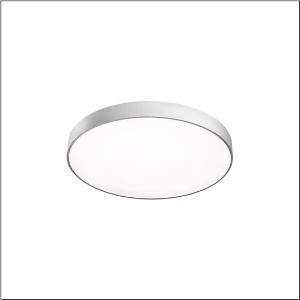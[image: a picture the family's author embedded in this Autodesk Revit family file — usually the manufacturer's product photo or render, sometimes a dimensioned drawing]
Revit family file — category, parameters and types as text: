
# Revit family: round_21_m_51mr36gm8321s
name_source: partatom
category: Lighting Fixtures
units: mm (PartAtom-declared; Revit-internal decimal feet)

## family parameters
Cut with Voids When Loaded = No
Host = Face
Light Source = No
Part Type = Normal
Room Calculation Point = No
Round Connector Dimension = Use Diameter
Shared = No

## types (1)
- --- (1 x LED, 7820 lm, 60.8 W, 3000K)
    Apparent Load = 61 VA
    CIE Flux Codes = 49 80 96 85 100
    Color Rendering = 80
    Color Temperature = 3000K
    Default Elevation = 1800 mm
    Description = Round 21 M, wall and ceiling luminaire, primary optical cover: cover, of PMMA, opal, light emission: direct/indirect distribution, primary light characteristic: symmetric, installation type: suspended mounting, surface-mounted, LED, rated luminous flux: 7.820lm, luminous efficacy: 129lm/W, light colour: 830, colour temperature: 3000K, with terminal, 3-pole, mains connection: 230V, AC, 50/60Hz, rated input power: 61W, housing, of aluminium, coated, silver, diameter: 600mm, height: 62mm, protection rating (complete): IP40, insulation class (complete): insulation class I (protective earthing), certification: CE, impact resistance: IK04, permissible operating ambient temperature: -10..+35°C, packaging unit: 1 piece
    Height = 87 mm
    Lamp = 1 x LED
    Lamp Light Flux = 7820 lm
    Lamp Power = 60.8 W
    Lamp count = 1
    Length = 600 mm
    Luminous efficacy = 129 lm/W
    Manufacturer = Siteco
    ModVariant = No
    Model = 51MR36GM8321S
    Mounting Place = Ceiling
    Mounting Type = Surface mounted
    Number of Poles = 1
    OnlyDefault = Yes
    Power Factor = 1
    Product Name = Round 21 M
    Product group = wall and ceiling luminaire
    ProductGroupID = 302
    Protection Class = Protection class I
    Protection Degree = IP 40
    RLX_Detail_Level = 1
    RLX_Emergency_Light_Flux = 0 lm
    RLX_Emergency_Type = 0
    RLX_Emergency_Type_DB = No
    RlxData = <blob elided: 17861 chars, md5=95593c90>
    Socket = socket
    Standby Power = 0 W
    System Light Flux = 7820 lm
    System Power = 61 W
    Type Comments = factory setting: luminous flux: 100 % | (ON | ON | ON | ON) | 700 mA
    Type Image = l_1258303.jpg
    URL = http://relux.com
    VarID = @adj_031823
    Voltage = 0 V
    Weight = 0.00 kg
    Width = 0 mm  [stored 0 ft]

note: [stored X ft] marks values corroborated as IEEE doubles in the binary element streams (Revit-internal decimal feet)

## geometry (parser evidence)
native form markers: Blend x4, Sweep x11
no freeform markers — native parametric forms only
